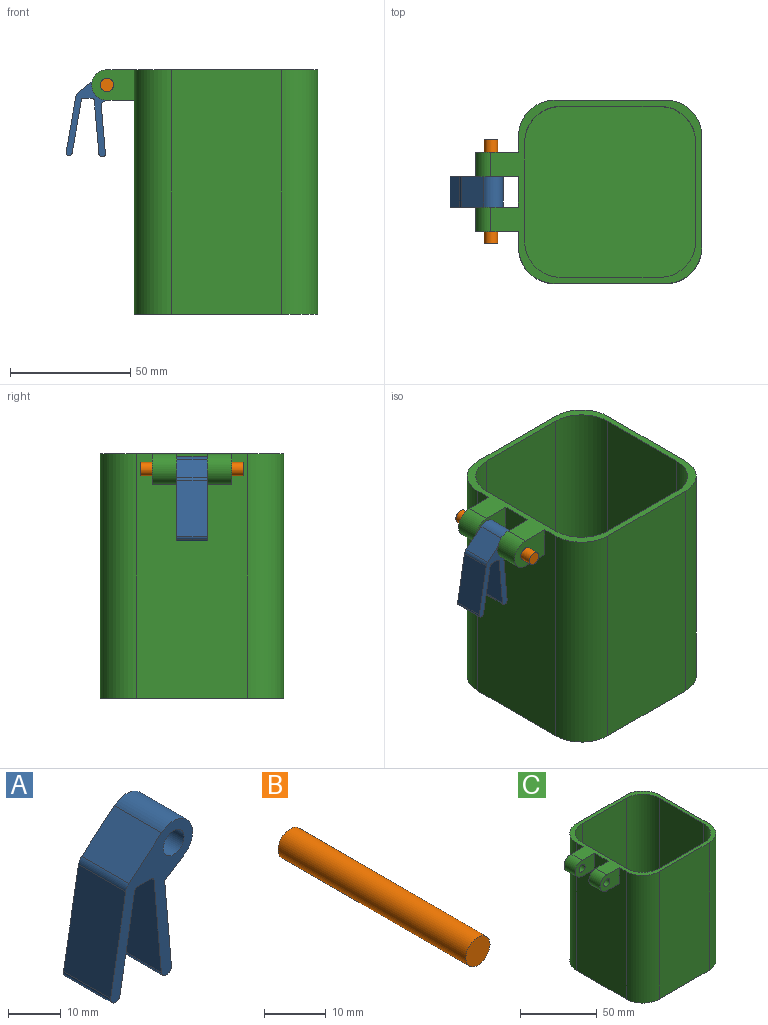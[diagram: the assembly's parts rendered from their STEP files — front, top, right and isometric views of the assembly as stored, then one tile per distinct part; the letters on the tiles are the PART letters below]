
ASSEMBLY  parts=3 mates=2
PART A: 16 faces, bbox 22.1x12.7x34.9 mm
  f0: cylinder r=0.85mm len=12.7mm, axis (0,1,0), area 16mm2, adj f1,f13,f14,f15
  f1: plane 22.4x12.7mm, normal (-1,0,-0.09), area 285.6mm2, adj f0,f2,f14,f15
  f2: cylinder r=1.36mm len=12.7mm, axis (0,1,0), area 54.1mm2, adj f1,f3,f14,f15
  f3: plane 20.77x12.7mm, normal (1,0,0.09), area 264.7mm2, adj f2,f4,f14,f15
  f4: plane 12.7x5.18mm, normal (0.54,0,-0.84), area 78.2mm2, adj f3,f5,f14,f15
  f5: cylinder r=5.08mm len=12.7mm, axis (0,1,0), area 210.9mm2, adj f4,f6,f14,f15
  f6: plane 12.7x8.78mm, normal (-0.64,0,0.77), area 145.6mm2, adj f5,f7,f14,f15
  f7: cylinder r=2.54mm len=12.7mm, axis (0,1,0), area 22.5mm2, adj f6,f8,f14,f15
  f8: plane 22.92x12.7mm, normal (-0.98,0,0.17), area 295.5mm2, adj f7,f9,f14,f15
  f9: cylinder r=1.27mm len=12.7mm, axis (0,1,0), area 50.7mm2, adj f8,f10,f14,f15
  f10: plane 22.21x12.7mm, normal (0.98,0,-0.17), area 286.5mm2, adj f9,f11,f14,f15
  f11: cylinder r=0.85mm len=12.7mm, axis (0,1,0), area 15.1mm2, adj f10,f13,f14,f15
  f12: cylinder r=2.79mm len=12.7mm, axis (0,1,0), area 223mm2, adj f14,f15
  f13: plane 12.7x3.58mm, normal (0,0,-1), area 45.4mm2, adj f0,f11,f14,f15
  f14: plane 34.92x22.06mm, normal (0,-1,0), area 231.2mm2, adj f0,f1,f2,f3,f4,f5,f6,f7
  f15: plane 34.92x22.06mm, normal (0,1,0), area 231.2mm2, adj f0,f1,f2,f3,f4,f5,f6,f7
PART B: 3 faces, bbox 5.6x43.2x5.6 mm
  f0: cylinder r=2.78mm len=43.18mm, axis (0,1,0), area 754.6mm2, adj f1,f2
  f1: plane 5.56x5.56mm, normal (0,-1,0), area 24.3mm2, adj f0
  f2: plane 5.56x5.56mm, normal (0,1,0), area 24.3mm2, adj f0
PART C: 29 faces, bbox 94x76.2x101.6 mm
  f0: plane 17.78x12.7mm, normal (0,-1,0), area 184mm2, adj f4,f6,f7,f26,f28
  f1: plane 17.78x12.7mm, normal (0,1,0), area 184mm2, adj f4,f6,f7,f26,f28
  f2: plane 17.78x12.7mm, normal (0,-1,0), area 184mm2, adj f5,f6,f7,f25,f27
  f3: plane 17.78x12.7mm, normal (0,1,0), area 184mm2, adj f5,f6,f7,f25,f27
  f4: plane 11.43x10.16mm, normal (0,0,-1), area 116.1mm2, adj f0,f1,f6,f26
  f5: plane 11.43x10.16mm, normal (0,0,-1), area 116.1mm2, adj f2,f3,f6,f25
  f6: plane 101.6x45.72mm, normal (-1,0,0), area 4387.1mm2, adj f0,f1,f2,f3,f4,f5,f7,f8
  f7: plane 87.63x76.2mm, normal (0,0,1), area 980.6mm2, adj f0,f1,f2,f3,f6,f9,f10,f11
  f8: plane 76.2x76.2mm, normal (0,0,-1), area 5607.1mm2, adj f6,f9,f10,f11,f21,f22,f23,f24
  f9: plane 101.6x45.72mm, normal (1,0,0), area 4645.2mm2, adj f7,f8,f21,f23
  f10: plane 101.6x45.72mm, normal (0,-1,0), area 4645.2mm2, adj f7,f8,f23,f24
  f11: plane 101.6x45.72mm, normal (0,1,0), area 4645.2mm2, adj f7,f8,f21,f22
  f12: plane 99.06x40.64mm, normal (1,0,0), area 4025.8mm2, adj f7,f13,f17,f19
  f13: plane 71.12x71.12mm, normal (0,0,1), area 4858.7mm2, adj f12,f14,f15,f16,f17,f18,f19,f20
  f14: plane 99.06x40.64mm, normal (-1,0,0), area 4025.8mm2, adj f7,f13,f18,f20
  f15: plane 99.06x40.64mm, normal (0,1,0), area 4025.8mm2, adj f7,f13,f17,f20
  f16: plane 99.06x40.64mm, normal (0,-1,0), area 4025.8mm2, adj f7,f13,f18,f19
  f17: cylinder r=15.24mm len=99.06mm, axis (0,0,-1), area 2371.4mm2, adj f7,f12,f13,f15
  f18: cylinder r=15.24mm len=99.06mm, axis (0,0,-1), area 2371.4mm2, adj f7,f13,f14,f16
  f19: cylinder r=15.24mm len=99.06mm, axis (0,0,1), area 2371.4mm2, adj f7,f12,f13,f16
  f20: cylinder r=15.24mm len=99.06mm, axis (0,0,1), area 2371.4mm2, adj f7,f13,f14,f15
  f21: cylinder r=15.24mm len=101.6mm, axis (0,0,1), area 2432.2mm2, adj f7,f8,f9,f11
  f22: cylinder r=15.24mm len=101.6mm, axis (0,0,-1), area 2432.2mm2, adj f6,f7,f8,f11
  f23: cylinder r=15.24mm len=101.6mm, axis (0,0,-1), area 2432.2mm2, adj f7,f8,f9,f10
  f24: cylinder r=15.24mm len=101.6mm, axis (0,0,1), area 2432.2mm2, adj f6,f7,f8,f10
  f25: cylinder r=6.35mm len=12.7mm, axis (0,-1,0), area 202.7mm2, adj f2,f3,f5,f7
  f26: cylinder r=6.35mm len=12.7mm, axis (0,-1,0), area 202.7mm2, adj f0,f1,f4,f7
  f27: cylinder r=2.79mm len=10.16mm, axis (0,-1,0), area 178.4mm2, adj f2,f3
  f28: cylinder r=2.79mm len=10.16mm, axis (0,-1,0), area 178.4mm2, adj f0,f1
PLACE A t=(46.66,7.53,27.83)mm fixed
PLACE B rot(axis=(0,1,0),90deg) t=(-45.78,22.77,-39.19)mm
PLACE C rot(axis=(0,-1,0),0deg) t=(-16.68,39.28,6.44)mm
MATE cylindrical B.f0 <-> C.f25  axis (0,-1,0) through (6.62,-20.41,12.89)mm
MATE revolute A.f5 <-> C.f25  axis (0,-1,0) through (6.62,-5.17,12.89)mm
